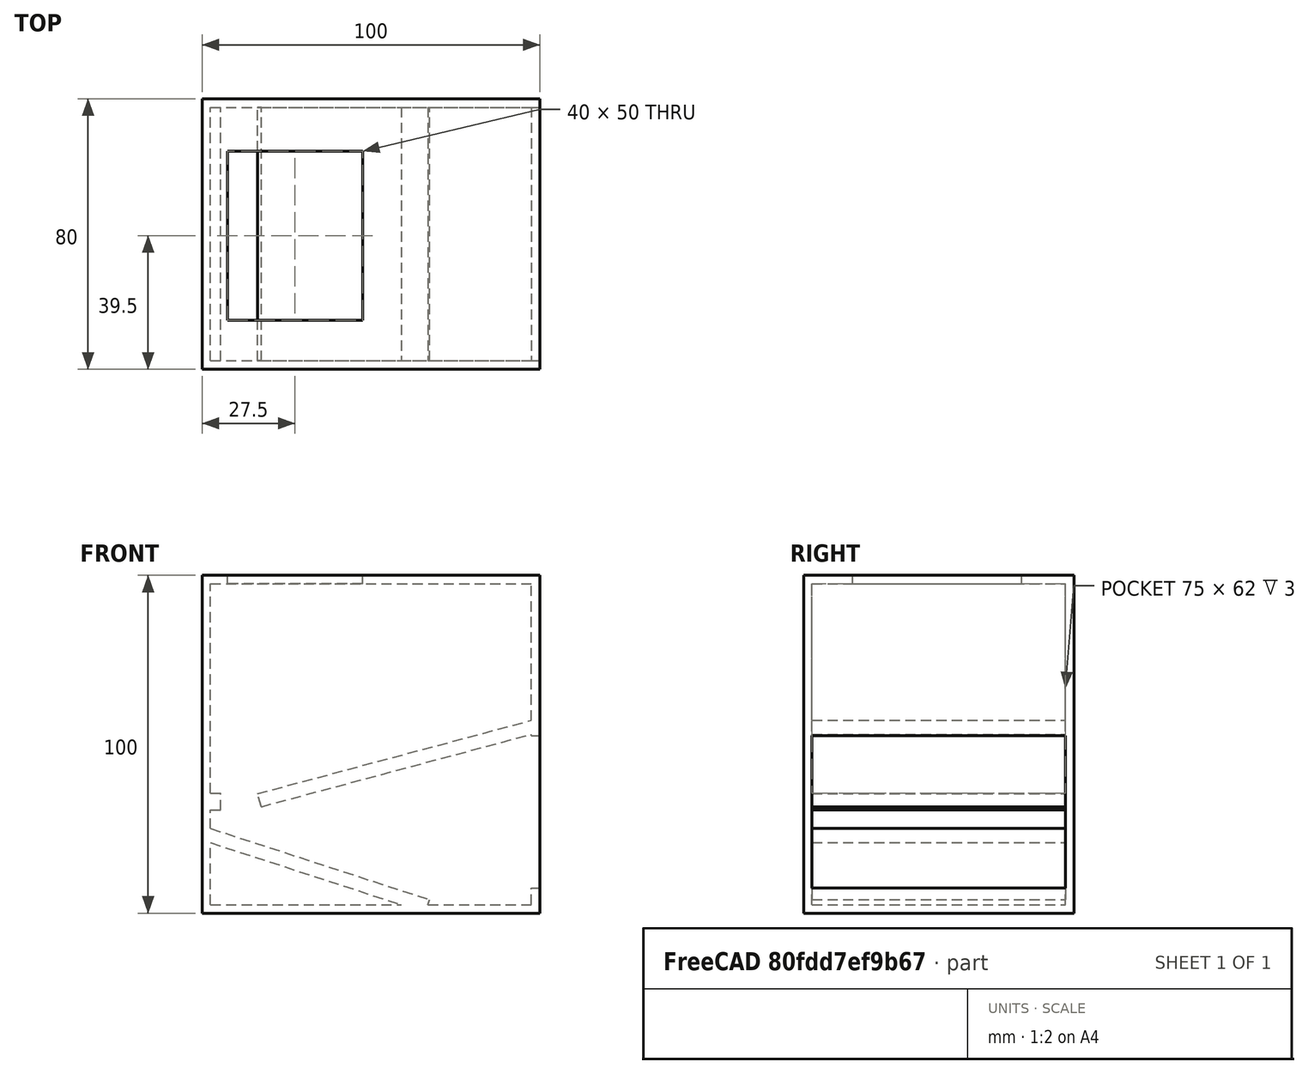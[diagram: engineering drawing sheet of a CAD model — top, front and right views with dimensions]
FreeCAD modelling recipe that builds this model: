
FCSTD DOCUMENT  (FreeCAD 0.16R6706 (Git))
Label: Petbuddy
License: All rights reserved
LicenseURL: http://en.wikipedia.org/wiki/All_rights_reserved
objects: Part::Box×7, Part::Cut×3, Part::MultiFuse×3
note: 13 computed .brp shape members not serialized (recipe doc carries the construction recipe); baked Part::Feature solids carry a one-line shape summary decoded from their .brp

FEATURE [Part::Box] Box  label="Cube"
  Height = 100
  Length = 100
  Placement = pos=(-2.5,-2.5,-2.5) rot=(0,0,1;0rad)
  Width = 80
FEATURE [Part::Box] Box001  label="inside hole"
  Height = 95
  Length = 95
  Width = 75
FEATURE [Part::Cut] Cut
  Base = -> Box
  Tool = -> Box001
FEATURE [Part::Box] Box002  label="Cube001"
  Height = 5
  Length = 40
  Placement = pos=(5,12,94) rot=(0,0,1;0rad)
  Width = 50
FEATURE [Part::Cut] Cut001
  Base = -> Cut
  Tool = -> Box002
FEATURE [Part::Box] Box003  label="Cube002"
  Height = 4
  Length = 84
  Placement = pos=(15,0,29) rot=(0,-1,0;0.261799rad)
  Width = 75
FEATURE [Part::MultiFuse] Fusion
  Shapes = -> [Box003,Cut001]
FEATURE [Part::Box] Box004  label="Cube003"
  Height = 5
  Length = 3
  Placement = pos=(0,0,28) rot=(0,0,1;0rad)
  Width = 75
FEATURE [Part::MultiFuse] Fusion001
  Shapes = -> [Box004,Fusion]
FEATURE [Part::Box] Box005  label="Cube004"
  Height = 4
  Length = 69
  Placement = pos=(-2,0,19) rot=(0,1,0;0.314159rad)
  Width = 75
FEATURE [Part::MultiFuse] Fusion002
  Shapes = -> [Box005,Fusion001]
FEATURE [Part::Box] Box006  label="Cube005"
  Height = 45
  Length = 9
  Placement = pos=(94,0,5) rot=(0,0,1;0rad)
  Width = 75
FEATURE [Part::Cut] Cut002  label="Compartment"
  Base = -> Fusion002
  Tool = -> Box006
